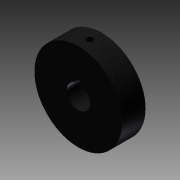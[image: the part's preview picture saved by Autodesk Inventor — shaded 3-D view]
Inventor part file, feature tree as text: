
AUTODESK INVENTOR PART (.ipt)
format: ipt  version: 2012 (Build 160160000, 160)  size: 105,472 bytes
history: native  units: in
note: dims shown in document units (in); Inventor stores cm internally (conversion verified against a paired STEP export)
features: extrude x2, sketch x2, plane x1, projected_geometry x1
ambient origin geometry x8: Origin, YZ Plane, XZ Plane, XY Plane, X Axis, Y Axis, Z Axis, Center Point
bodies: Solid1 (feature_tree)
feature tree (6):
  extrude  "Extrusion1"  Depth=0.5in
  plane  "Work Plane1"
  extrude  "Extrusion2"  Depth=0.0625in
  sketch  "Sketch1"  dims[d0=1.875in d1=0.5in]
  sketch  "Sketch2"  dims[d2=0.125in d3=0.0625in d4=0.3125in d5=0.5in d6=0.0in d7=0.136in d8=0.25in d9=0.9375in d10=1.0in d11=0.0in]
  projected_geometry  "Projected Loop1"
